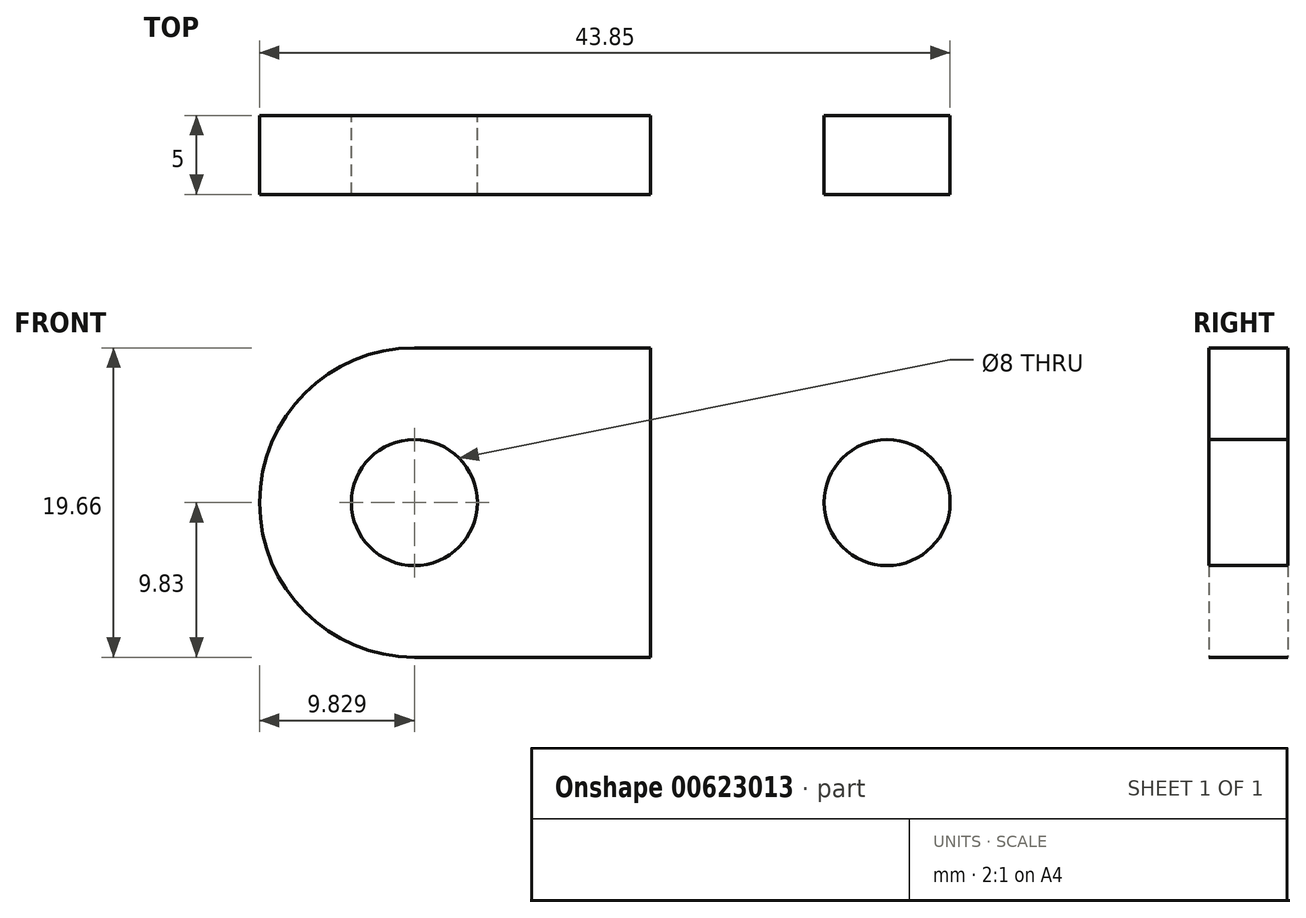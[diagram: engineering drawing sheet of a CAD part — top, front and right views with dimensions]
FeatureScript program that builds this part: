
annotation { "Feature Type Name" : "Feature", "Feature Type Description" : "" }
export const myFeature = defineFeature(function(context is Context, id is Id, definition is map)
    precondition{}
    {
        {
            var Q0;
            Q0=qCreatedBy(makeId("Front.planeOp"),FACE);
            var sketch = newSketch(context, id + "F0", { "sketchPlane" : qUnion([Q0])});
            skLineSegment(sketch, "E0", {"start": v(-15.01, 0) * mm, "end": v(0, 0) * mm});
            skLineSegment(sketch, "E1", {"start": v(0, 14.34) * mm, "end": v(0, -12.95) * mm});
            skArc(sketch, "E2", {"start": v(-15.01, 9.83) * mm, "mid": v(-24.84, 0) * mm, "end": v(-15.01, -9.83) * mm});
            skLineSegment(sketch, "E3.0", {"start": v(-15.01, -9.83) * mm, "end": v(0, -9.83) * mm});
            skLineSegment(sketch, "E4", {"start": v(-15.01, 9.83) * mm, "end": v(0, 9.83) * mm});
            skCircle(sketch, "E5", {"center": v(-15.01, 0) * mm, "radius": 4 * mm});
            skCircle(sketch, "E6.MirrorC", {"center": v(15.01, 0) * mm, "radius": 4 * mm});
            skLineSegment(sketch, "E7.MirrorCS", {"start": v(15.01, 9.83) * mm, "end": v(0, 9.83) * mm});
            skLineSegment(sketch, "E8.MirrorCS", {"start": v(15.01, -9.83) * mm, "end": v(0, -9.83) * mm});
            skLineSegment(sketch, "E9.MirrorCS", {"start": v(15.01, 0) * mm, "end": v(0, 0) * mm});
            skArc(sketch, "E10.MirrorCS", {"start": v(15.01, 9.83) * mm, "mid": v(24.84, 0) * mm, "end": v(15.01, -9.83) * mm});
            skSolve(sketch);
        }
        {
            var Q0;
            Q0=makeQuery(id+"F0.imprint","IMPRINT",FACE,{"disambiguationData":[TD([[makeQuery(id+"F0.imprint","IMPRINT",EDGE,{"derivedFrom":sQuery(id+"F0.wireOp",EDGE,"E6.MirrorC")}),1.0]])]});
            var Q1;
            Q1=makeQuery(id+"F0.imprint","IMPRINT",FACE,{"disambiguationData":[TD([[makeQuery(id+"F0.imprint","IMPRINT",EDGE,{"derivedFrom":sQuery(id+"F0.wireOp",EDGE,"E2")}),1.0]])]});
            extrude(context, id + "F1", {"entities" : qUnion([Q0, Q1]), "endBound" : BoundingType.SYMMETRIC, "depth" : 5 * mm, "offsetDistance" : 25.4 * mm});
        }
    });
